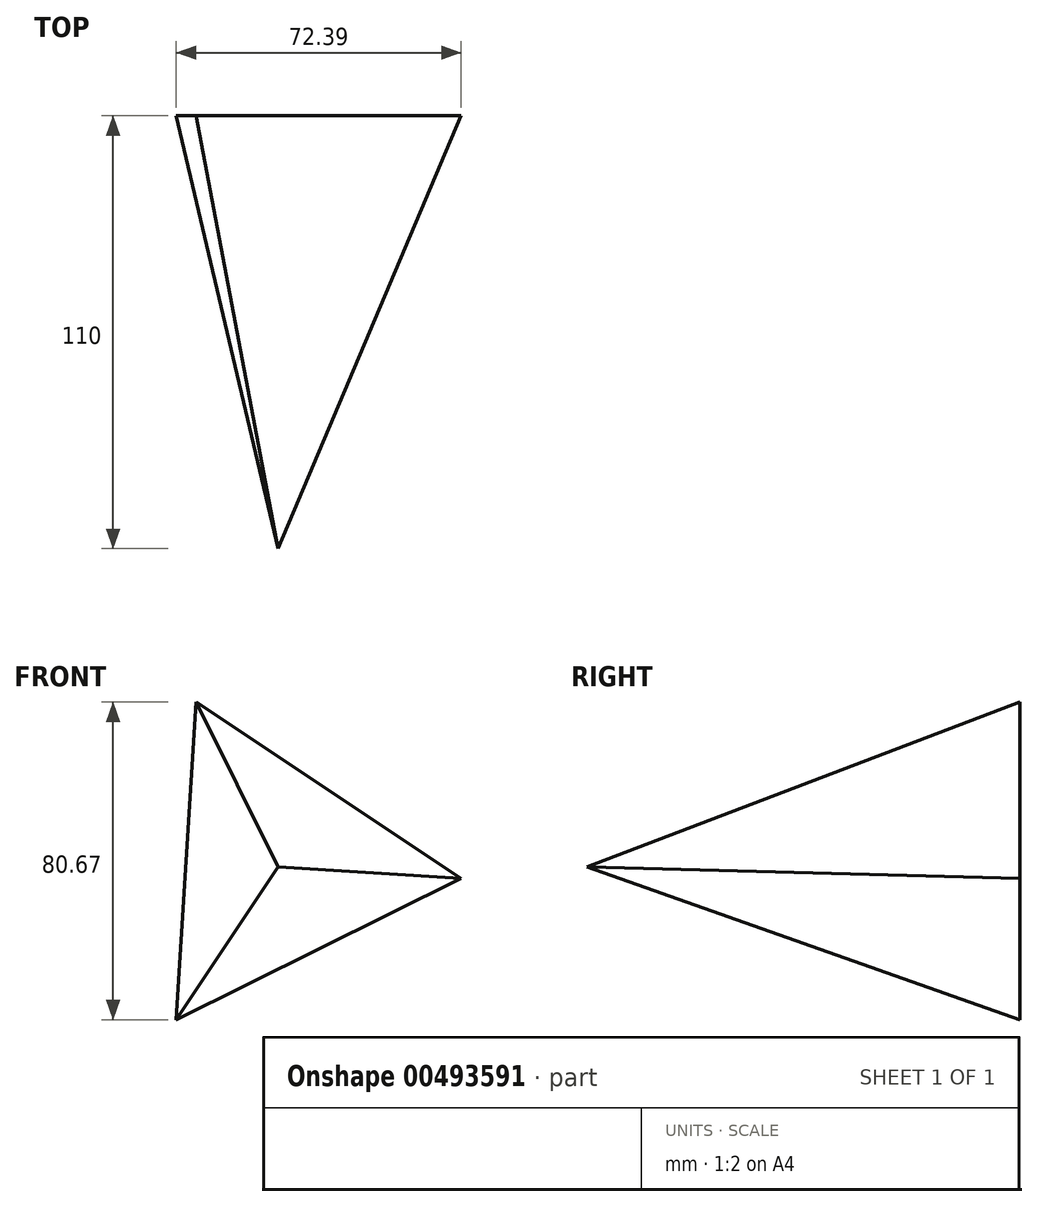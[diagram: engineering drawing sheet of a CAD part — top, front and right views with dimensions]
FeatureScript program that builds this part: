
annotation { "Feature Type Name" : "Feature", "Feature Type Description" : "" }
export const myFeature = defineFeature(function(context is Context, id is Id, definition is map)
    precondition{}
    {
        {
            var Q0;
            Q0=qCreatedBy(makeId("Front.planeOp"),FACE);
            var sketch = newSketch(context, id + "F0", { "sketchPlane" : qUnion([Q0])});
            skCircle(sketch, "E0.cCircle", {"center": v(0, 0) * mm, "radius": 46.67 * mm, "construction": true});
            skLineSegment(sketch, "E0.0", {"start": v(-25.82, -38.87) * mm, "end": v(-20.76, 41.8) * mm});
            skLineSegment(sketch, "E0.1", {"start": v(-20.76, 41.8) * mm, "end": v(46.57, -2.92) * mm});
            skLineSegment(sketch, "E0.2", {"start": v(46.57, -2.92) * mm, "end": v(-25.82, -38.87) * mm});
            skSolve(sketch);
        }
        {
            var Q0;
            Q0=qCreatedBy(makeId("Front.planeOp"),FACE);
            cPlane(context, id + "F1", {"entities" : qUnion([Q0]), "cplaneType" : CPlaneType.OFFSET, "offset" : 110 * mm, "width" : 150 * mm, "height" : 150 * mm});
        }
        {
            var Q0;
            Q0=qCreatedBy(id+"F1.planeOp",FACE);
            var sketch = newSketch(context, id + "F2", { "sketchPlane" : qUnion([Q0])});
            skPoint(sketch, "E1", {"position": v(0, 0) * mm});
            skSolve(sketch);
        }
        {
            var Q0;
            Q0=makeQuery(id+"F0.imprint","IMPRINT",FACE,{"disambiguationData":[TD([[makeQuery(id+"F0.imprint","IMPRINT",EDGE,{"derivedFrom":sQuery(id+"F0.wireOp",EDGE,"E0.0")}),-1.0]])]});
            var Q1;
            Q1=sQuery(id+"F2.wireOp",VERTEX,"E1");
            loft(context, id + "F3", {"sheetProfilesArray" : [{ "sheetProfileEntities" : qUnion([Q0]) }, { "sheetProfileEntities" : qUnion([Q1]) }]});
        }
    });
